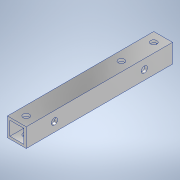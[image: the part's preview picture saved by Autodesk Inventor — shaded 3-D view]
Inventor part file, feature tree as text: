
AUTODESK INVENTOR PART (.ipt)
format: ipt  version: 2020.3 (Build 243373000, 373)  size: 135,680 bytes
history: native  units: mm
features: sketch x4, hole x3, other x1, extrude x1
ambient origin geometry x8: Origin, YZ Plane, XZ Plane, XY Plane, X Axis, Y Axis, Z Axis, Center Point
bodies: Body1 (feature_tree)
feature tree (9):
  other  "ソリッド1"
  extrude  "押し出し1"  Depth=9.0mm
  hole  "穴2"  [1 undecoded]
  hole  "穴3"  [1 undecoded]
  hole  "穴4"  [1 undecoded]
  sketch  "スケッチ1"
  sketch  "スケッチ3"
  sketch  "スケッチ4"
  sketch  "スケッチ5"
note: 3 required parameter values undecoded (feature->parameter linkage not recoverable at this tier; creation-order binding heuristic only, values carry confidence <= 0.55)
